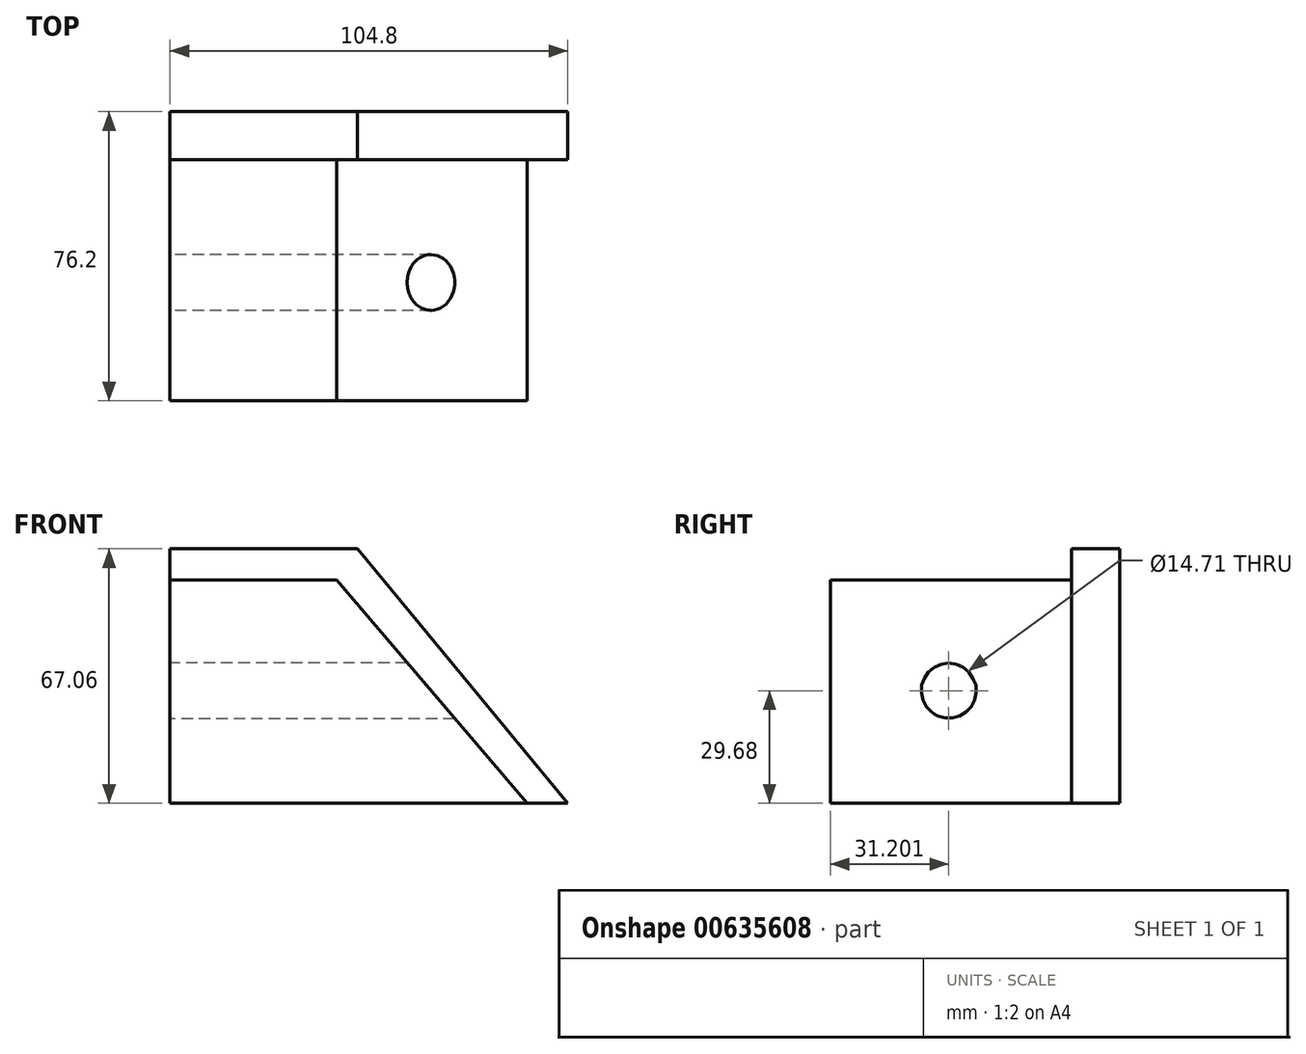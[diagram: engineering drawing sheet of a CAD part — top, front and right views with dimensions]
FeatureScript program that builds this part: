
annotation { "Feature Type Name" : "Feature", "Feature Type Description" : "" }
export const myFeature = defineFeature(function(context is Context, id is Id, definition is map)
    precondition{}
    {
        {
            var Q0;
            Q0=qCreatedBy(makeId("Front.planeOp"),FACE);
            var sketch = newSketch(context, id + "F0", { "sketchPlane" : qUnion([Q0])});
            skLineSegment(sketch, "E0", {"start": v(0, 0) * mm, "end": v(0, 67.06) * mm});
            skLineSegment(sketch, "E1", {"start": v(0, 67.06) * mm, "end": v(49.44, 67.06) * mm});
            skLineSegment(sketch, "E2", {"start": v(49.44, 67.06) * mm, "end": v(104.8, 0) * mm});
            skLineSegment(sketch, "E3", {"start": v(104.8, 0) * mm, "end": v(0, 0) * mm});
            skLineSegment(sketch, "E4", {"start": v(0, 58.8) * mm, "end": v(43.93, 58.8) * mm});
            skLineSegment(sketch, "E5", {"start": v(43.93, 58.8) * mm, "end": v(94.06, 0) * mm});
            skSolve(sketch);
        }
        {
            var Q0;
            {var subQ3=sQuery(id+"F0.wireOp",EDGE,"E4");Q0=makeQuery(id+"F0.imprint","IMPRINT",FACE,{"disambiguationData":[TD([[makeQuery(id+"F0.imprint","IMPRINT",EDGE,{"derivedFrom":subQ3}),-1.0]])]});}
            extrude(context, id + "F1", {"entities" : qUnion([Q0]), "depth" : 76.2 * mm, "offsetDistance" : 25.4 * mm});
        }
        {
            var Q0;
            {var subQ3=sQuery(id+"F0.wireOp",EDGE,"E1");Q0=makeQuery(id+"F0.imprint","IMPRINT",FACE,{"disambiguationData":[TD([[makeQuery(id+"F0.imprint","IMPRINT",EDGE,{"derivedFrom":subQ3}),-1.0]])]});}
            extrude(context, id + "F2", {"entities" : qUnion([Q0]), "operationType" : NewBodyOperationType.ADD, "depth" : 12.7 * mm, "offsetDistance" : 25.4 * mm});
        }
        {
            var Q0;
            Q0=qCreatedBy(makeId("Right.planeOp"),FACE);
            var sketch = newSketch(context, id + "F3", { "sketchPlane" : qUnion([Q0])});
            skCircle(sketch, "E6", {"center": v(-45, 29.68) * mm, "radius": 7.36 * mm});
            skSolve(sketch);
        }
        {
            var Q0;
            Q0 = qSketchRegion(id + "F3", true);
            extrude(context, id + "F4", {"entities" : qUnion([Q0]), "operationType" : NewBodyOperationType.REMOVE, "endBound" : BoundingType.THROUGH_ALL, "depth" : 25.4 * mm, "offsetDistance" : 25.4 * mm});
        }
    });
